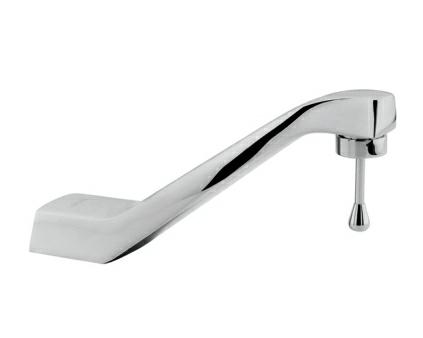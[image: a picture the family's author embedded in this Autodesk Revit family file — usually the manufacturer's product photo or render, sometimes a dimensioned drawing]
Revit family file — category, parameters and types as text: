
# Revit family: TV-105_RFA
name_source: partatom
category: Aparatos sanitarios
units: mm (PartAtom-declared; Revit-internal decimal feet)

## family parameters
Compartido = Sí
Corte con vacíos al cargar = No
Cota de conector redondo = Diámetro de uso
Número OmniClass = 23.45.00.00
Punto de cálculo de habitación = Sí
Se basa en plano de trabajo = Sí
Siempre vertical = Sí
Tipo de pieza = Normal
Título OmniClass = Sanitary, Laundry, and Cleaning Equipment

## types (1)
- TV-105
    Accessories = Economizador para autoajuste de flujo y palanca con recubrimiento antibacterial
    Chrome = Brass Chromed
    Comentarios de tipo = Llave Economizadora
    Compliance = NMX-C-415-ONNCCE-1999
    Connection = ½" - 14 NPSM
    Descripción = Llave Economizadora con Seguro Antirrobo
    Elevación por Defecto = 1"
    Elevación por defecto = 48"
    Fabricante = HELVEX S.A. DE C.V.
    Imagen de tipo = TV-105.jpg
    Max. Water Flow = 1.2 gal/min
    Max. Working Pressure = 85.3 psi
    Min. Working Pressure = 2.8 psi
    Modelo = TV-105
    Operation = Cierre Automático y Perilla multidireccional
    Total Height = 4"
    Total Length = 6"
    Total Width = 2"
    URL = http://www.helvex.com.mx
    Warranty = El producto HELVEX está garantizado como libre de defectos en materiales y procesos de fabricación. El producto HELVEX está garantizado, en lo que se refiere a los acabados; por un periodo de 10 años en los acabados cromo y duravex, y por 2 años en cabados diferentes al cromo, a partir de la fecha de compra indicada en la factura.

## geometry (parser evidence)
native form markers: Sweep x3
no freeform markers — native parametric forms only
